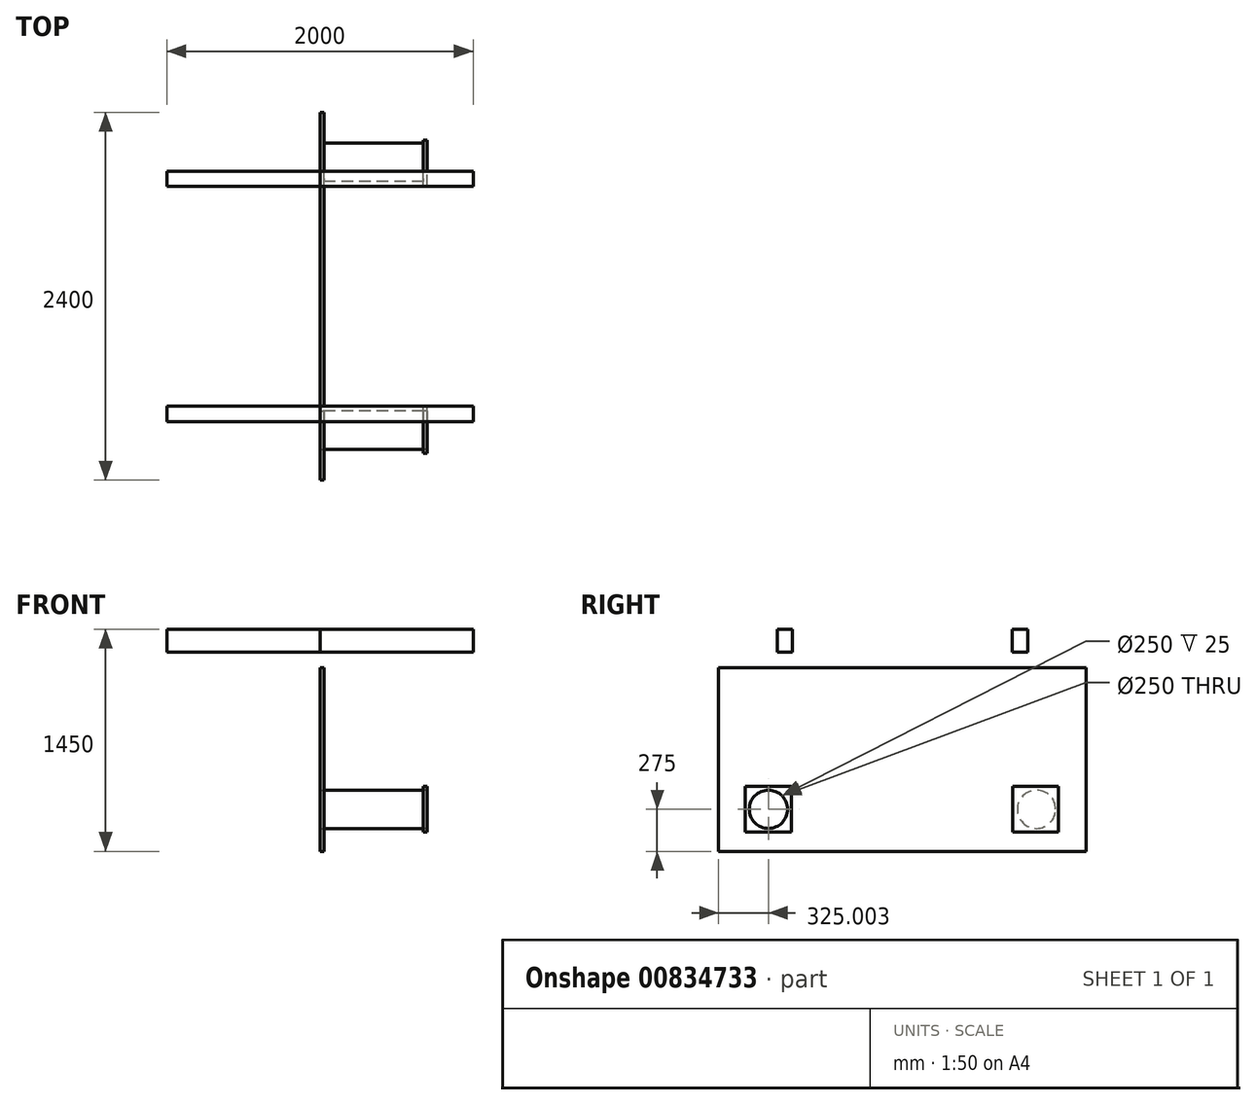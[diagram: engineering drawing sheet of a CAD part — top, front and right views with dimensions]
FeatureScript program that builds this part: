
annotation { "Feature Type Name" : "Feature", "Feature Type Description" : "" }
export const myFeature = defineFeature(function(context is Context, id is Id, definition is map)
    precondition{}
    {
        {
            var Q0;
            Q0=qCreatedBy(makeId("Right.planeOp"),FACE);
            var sketch = newSketch(context, id + "F0", { "sketchPlane" : qUnion([Q0])});
            skLineSegment(sketch, "E0", {"start": v(-67.14, 0) * mm, "end": v(1682.86, 0) * mm});
            skCircle(sketch, "E1", {"center": v(-67.14, 0) * mm, "radius": 125 * mm});
            skCircle(sketch, "E2", {"center": v(1682.86, 0) * mm, "radius": 125 * mm});
            skSolve(sketch);
        }
        {
            var Q0;
            Q0=makeQuery(id+"F0.imprint","IMPRINT",FACE,{"disambiguationData":[TD([[makeQuery(id+"F0.imprint","IMPRINT",EDGE,{"derivedFrom":sQuery(id+"F0.wireOp",EDGE,"E1")}),1.0]])]});
            var Q1;
            Q1=makeQuery(id+"F0.imprint","IMPRINT",FACE,{"disambiguationData":[TD([[makeQuery(id+"F0.imprint","IMPRINT",EDGE,{"derivedFrom":sQuery(id+"F0.wireOp",EDGE,"E2")}),1.0]])]});
            extrude(context, id + "F1", {"entities" : qUnion([Q0, Q1]), "depth" : 650 * mm, "offsetDistance" : 25 * mm});
        }
        {
            var Q0;
            Q0=makeQuery(id+"F1.opExtrude","CAP_FACE",FACE,{"disambiguationData":[OSD([sQuery(id+"F0.wireOp",EDGE,"E1")])],"isStart":false});
            var sketch = newSketch(context, id + "F2", { "sketchPlane" : qUnion([Q0])});
            skLineSegment(sketch, "E3.bottom", {"start": v(-217.14, 150) * mm, "end": v(82.86, 150) * mm});
            skLineSegment(sketch, "E3.top", {"start": v(-217.14, -150) * mm, "end": v(82.86, -150) * mm});
            skLineSegment(sketch, "E3.left", {"start": v(-217.14, 150) * mm, "end": v(-217.14, -150) * mm});
            skLineSegment(sketch, "E3.right", {"start": v(82.86, 150) * mm, "end": v(82.86, -150) * mm});
            skPoint(sketch, "E3.middle", {"position": v(-67.14, 0) * mm});
            skLineSegment(sketch, "E4.bottom", {"start": v(1526.55, 150) * mm, "end": v(1826.55, 150) * mm});
            skLineSegment(sketch, "E4.top", {"start": v(1526.55, -150) * mm, "end": v(1826.55, -150) * mm});
            skLineSegment(sketch, "E4.left", {"start": v(1526.55, 150) * mm, "end": v(1526.55, -150) * mm});
            skLineSegment(sketch, "E4.right", {"start": v(1826.55, 150) * mm, "end": v(1826.55, -150) * mm});
            skPoint(sketch, "E4.middle", {"position": v(1676.55, 0) * mm});
            skSolve(sketch);
        }
        {
            var Q0;
            Q0=makeQuery(id+"F2.imprint","IMPRINT",FACE,{"disambiguationData":[TD([[makeQuery(id+"F2.imprint","IMPRINT",EDGE,{"derivedFrom":sQuery(id+"F2.wireOp",EDGE,"E4.bottom")}),-1.0]])]});
            var Q1;
            Q1=makeQuery(id+"F2.imprint","IMPRINT",FACE,{"disambiguationData":[TD([[makeQuery(id+"F2.imprint","IMPRINT",EDGE,{"derivedFrom":sQuery(id+"F2.wireOp",EDGE,"E3.bottom")}),-1.0]])]});
            extrude(context, id + "F3", {"entities" : qUnion([Q0, Q1]), "depth" : 25 * mm, "offsetDistance" : 25 * mm});
        }
        {
            var Q0;
            Q0=makeQuery(id+"F1.opExtrude","SWEPT_BODY",BODY,{"disambiguationData":[OSD([sQuery(id+"F0.wireOp",EDGE,"E1")])]});
            var Q1;
            Q1=makeQuery(id+"F3.opExtrude","SWEPT_BODY",BODY,{"disambiguationData":[OSD([sQuery(id+"F0.wireOp",EDGE,"E1"),sQuery(id+"F2.wireOp",EDGE,"E3.bottom"),sQuery(id+"F2.wireOp",EDGE,"E3.top"),sQuery(id+"F2.wireOp",EDGE,"E3.left"),sQuery(id+"F2.wireOp",EDGE,"E3.right")])]});
            var Q2;
            Q2=makeQuery(id+"F3.opExtrude","SWEPT_BODY",BODY,{"disambiguationData":[OSD([sQuery(id+"F2.wireOp",EDGE,"E4.bottom"),sQuery(id+"F2.wireOp",EDGE,"E4.top"),sQuery(id+"F2.wireOp",EDGE,"E4.left"),sQuery(id+"F2.wireOp",EDGE,"E4.right")])]});
            var Q3;
            Q3=makeQuery(id+"F1.opExtrude","SWEPT_BODY",BODY,{"disambiguationData":[OSD([sQuery(id+"F0.wireOp",EDGE,"E2")])]});
            booleanBodies(context, id + "F4", {"operationType" : BooleanOperationType.UNION, "tools" : qUnion([Q0, Q1, Q2, Q3])});
        }
        {
            var Q0;
            Q0=makeQuery(id+"F1.opExtrude","CAP_FACE",FACE,{"disambiguationData":[OSD([sQuery(id+"F0.wireOp",EDGE,"E1")])],"isStart":true});
            var sketch = newSketch(context, id + "F5", { "sketchPlane" : qUnion([Q0])});
            skLineSegment(sketch, "E5.bottom", {"start": v(392.14, 925) * mm, "end": v(-2007.86, 925) * mm});
            skLineSegment(sketch, "E5.top", {"start": v(392.14, -275) * mm, "end": v(-2007.86, -275) * mm});
            skLineSegment(sketch, "E5.left", {"start": v(392.14, 925) * mm, "end": v(392.14, -275) * mm});
            skLineSegment(sketch, "E5.right", {"start": v(-2007.86, 925) * mm, "end": v(-2007.86, -275) * mm});
            skSolve(sketch);
        }
        {
            var Q0;
            Q0=makeQuery(id+"F5.imprint","IMPRINT",FACE,{"disambiguationData":[TD([[makeQuery(id+"F5.imprint","IMPRINT",EDGE,{"derivedFrom":sQuery(id+"F5.wireOp",EDGE,"E5.bottom")}),1.0]])]});
            extrude(context, id + "F6", {"entities" : qUnion([Q0]), "operationType" : NewBodyOperationType.ADD, "depth" : 25 * mm, "offsetDistance" : 25 * mm});
        }
        {
            var Q0;
            Q0=makeQuery(id+"F6.opExtrude","CAP_FACE",FACE,{"disambiguationData":[OSD([sQuery(id+"F0.wireOp",EDGE,"E1"),sQuery(id+"F5.wireOp",EDGE,"E5.bottom"),sQuery(id+"F5.wireOp",EDGE,"E5.top"),sQuery(id+"F5.wireOp",EDGE,"E5.left"),sQuery(id+"F5.wireOp",EDGE,"E5.right")])],"isStart":false});
            var sketch = newSketch(context, id + "F7", { "sketchPlane" : qUnion([Q0])});
            skLineSegment(sketch, "E6.bottom", {"start": v(9.64, 1025) * mm, "end": v(-90.36, 1025) * mm});
            skLineSegment(sketch, "E6.top", {"start": v(9.64, 1175) * mm, "end": v(-90.36, 1175) * mm});
            skLineSegment(sketch, "E6.left", {"start": v(9.64, 1025) * mm, "end": v(9.64, 1175) * mm});
            skLineSegment(sketch, "E6.right", {"start": v(-90.36, 1025) * mm, "end": v(-90.36, 1175) * mm});
            skLineSegment(sketch, "E7.bottom", {"start": v(-1525.36, 1175) * mm, "end": v(-1625.36, 1175) * mm});
            skLineSegment(sketch, "E7.top", {"start": v(-1525.36, 1025) * mm, "end": v(-1625.36, 1025) * mm});
            skLineSegment(sketch, "E7.left", {"start": v(-1525.36, 1175) * mm, "end": v(-1525.36, 1025) * mm});
            skLineSegment(sketch, "E7.right", {"start": v(-1625.36, 1175) * mm, "end": v(-1625.36, 1025) * mm});
            skPoint(sketch, "E8", {"position": v(67.14, 0) * mm});
            skLineSegment(sketch, "E9", {"start": v(67.14, 0) * mm, "end": v(-1682.86, 0) * mm});
            skPoint(sketch, "E10", {"position": v(-807.86, 0) * mm});
            skLineSegment(sketch, "E11", {"start": v(-807.86, 0) * mm, "end": v(-807.86, 925) * mm});
            skSolve(sketch);
        }
        {
            var Q0;
            Q0=makeQuery(id+"F7.imprint","IMPRINT",FACE,{"disambiguationData":[TD([[makeQuery(id+"F7.imprint","IMPRINT",EDGE,{"derivedFrom":sQuery(id+"F7.wireOp",EDGE,"E7.bottom")}),1.0]])]});
            var Q1;
            Q1=makeQuery(id+"F7.imprint","IMPRINT",FACE,{"disambiguationData":[TD([[makeQuery(id+"F7.imprint","IMPRINT",EDGE,{"derivedFrom":sQuery(id+"F7.wireOp",EDGE,"E6.bottom")}),-1.0]])]});
            extrude(context, id + "F8", {"entities" : qUnion([Q0, Q1]), "depth" : 1000 * mm, "offsetDistance" : 25 * mm});
        }
        {
            var Q0;
            Q0=makeQuery(id+"F7.imprint","IMPRINT",FACE,{"disambiguationData":[TD([[makeQuery(id+"F7.imprint","IMPRINT",EDGE,{"derivedFrom":sQuery(id+"F7.wireOp",EDGE,"E6.bottom")}),-1.0]])]});
            var Q1;
            Q1=makeQuery(id+"F7.imprint","IMPRINT",FACE,{"disambiguationData":[TD([[makeQuery(id+"F7.imprint","IMPRINT",EDGE,{"derivedFrom":sQuery(id+"F7.wireOp",EDGE,"E7.bottom")}),1.0]])]});
            extrude(context, id + "F9", {"entities" : qUnion([Q0, Q1]), "oppositeDirection" : true, "depth" : 1000 * mm, "offsetDistance" : 25 * mm});
        }
    });
